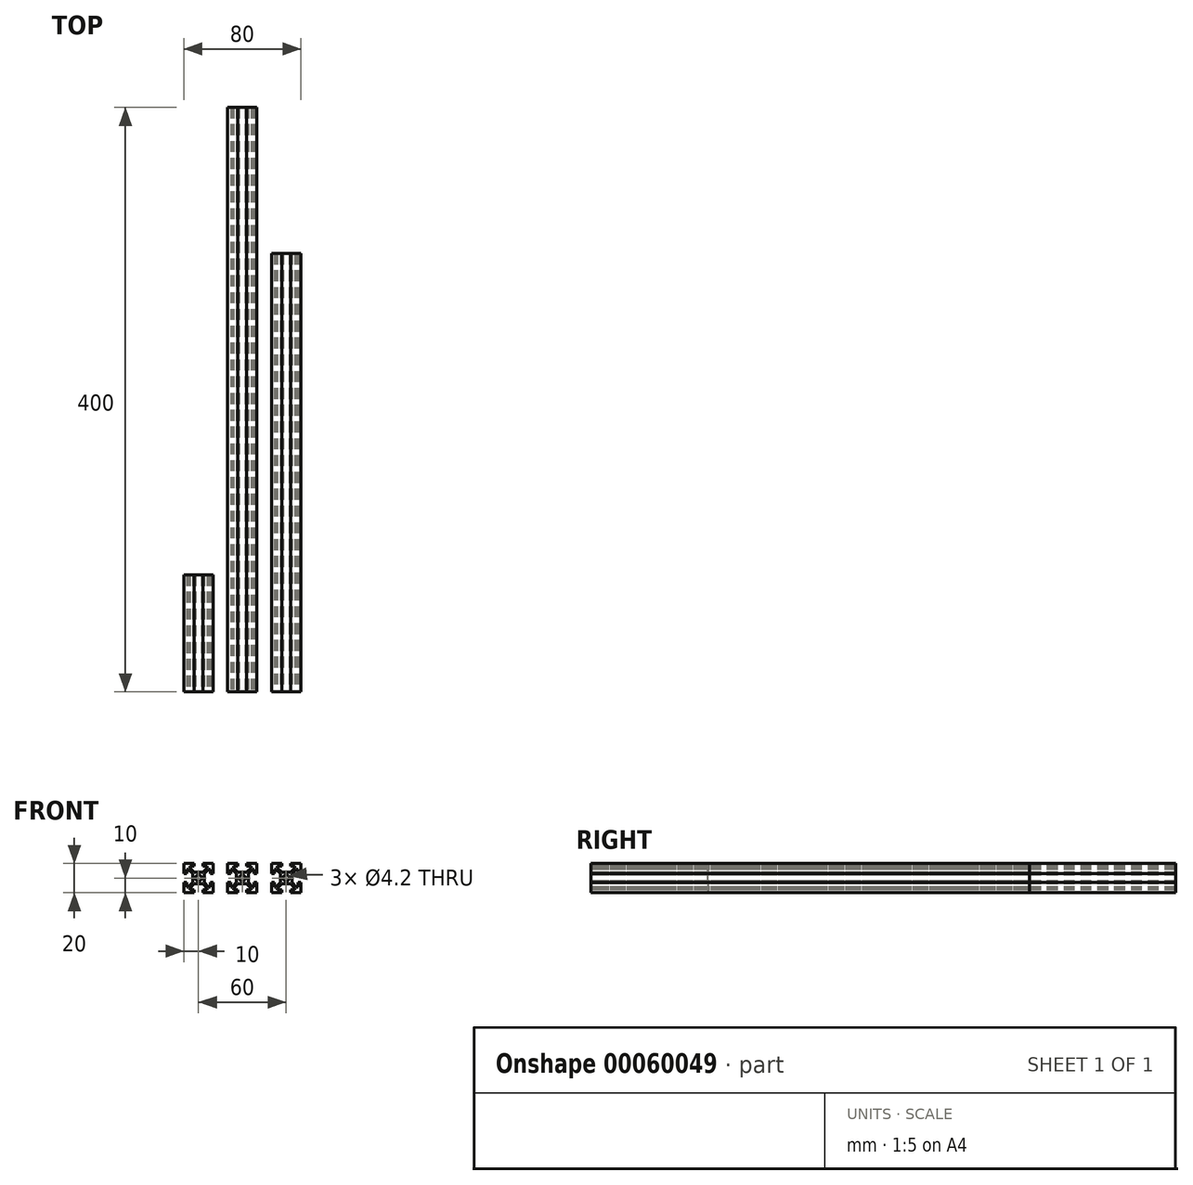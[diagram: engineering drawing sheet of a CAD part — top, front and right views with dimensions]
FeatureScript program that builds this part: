
annotation { "Feature Type Name" : "Feature", "Feature Type Description" : "" }
export const myFeature = defineFeature(function(context is Context, id is Id, definition is map)
    precondition{}
    {
        {
            var Q0;
            Q0=qCreatedBy(makeId("Front.planeOp"),FACE);
            var sketch = newSketch(context, id + "F0", { "sketchPlane" : qUnion([Q0])});
            skLineSegment(sketch, "E0", {"start": v(0, 4) * mm, "end": v(3, 4) * mm});
            skLineSegment(sketch, "E1", {"start": v(3, 4) * mm, "end": v(6, 7) * mm});
            skLineSegment(sketch, "E2", {"start": v(6, 7) * mm, "end": v(6, 8) * mm});
            skLineSegment(sketch, "E3", {"start": v(6, 8) * mm, "end": v(3, 8) * mm});
            skLineSegment(sketch, "E4", {"start": v(3, 8) * mm, "end": v(3, 10) * mm});
            skLineSegment(sketch, "E5", {"start": v(3, 10) * mm, "end": v(10, 10) * mm});
            skLineSegment(sketch, "E6", {"start": v(0, 0) * mm, "end": v(23.75, 23.75) * mm, "construction": true});
            skLineSegment(sketch, "E7.MirrorCS", {"start": v(8, 6) * mm, "end": v(8, 3) * mm});
            skLineSegment(sketch, "E8.MirrorCS", {"start": v(7, 6) * mm, "end": v(8, 6) * mm});
            skLineSegment(sketch, "E9.MirrorCS", {"start": v(8, 3) * mm, "end": v(10, 3) * mm});
            skLineSegment(sketch, "E10.MirrorCS", {"start": v(4, 0) * mm, "end": v(4, 3) * mm});
            skLineSegment(sketch, "E11.MirrorCS", {"start": v(10, 3) * mm, "end": v(10, 10) * mm});
            skLineSegment(sketch, "E12.MirrorCS", {"start": v(4, 3) * mm, "end": v(7, 6) * mm});
            skLineSegment(sketch, "E13.MirrorCS", {"start": v(-4, 3) * mm, "end": v(-7, 6) * mm});
            skLineSegment(sketch, "E14.MirrorCS", {"start": v(-10, 3) * mm, "end": v(-10, 10) * mm});
            skLineSegment(sketch, "E15.MirrorCS", {"start": v(-4, 0) * mm, "end": v(-4, 3) * mm});
            skLineSegment(sketch, "E16.MirrorCS", {"start": v(-8, 3) * mm, "end": v(-10, 3) * mm});
            skLineSegment(sketch, "E17.MirrorCS", {"start": v(-7, 6) * mm, "end": v(-8, 6) * mm});
            skLineSegment(sketch, "E18.MirrorCS", {"start": v(-8, 6) * mm, "end": v(-8, 3) * mm});
            skLineSegment(sketch, "E19.MirrorCS", {"start": v(-3, 10) * mm, "end": v(-10, 10) * mm});
            skLineSegment(sketch, "E20.MirrorCS", {"start": v(0, 4) * mm, "end": v(-3, 4) * mm});
            skLineSegment(sketch, "E21.MirrorCS", {"start": v(-3, 4) * mm, "end": v(-6, 7) * mm});
            skLineSegment(sketch, "E22.MirrorCS", {"start": v(-3, 8) * mm, "end": v(-3, 10) * mm});
            skLineSegment(sketch, "E23.MirrorCS", {"start": v(-6, 8) * mm, "end": v(-3, 8) * mm});
            skLineSegment(sketch, "E24.MirrorCS", {"start": v(-6, 7) * mm, "end": v(-6, 8) * mm});
            skLineSegment(sketch, "E25.MirrorCS", {"start": v(-6, -7) * mm, "end": v(-6, -8) * mm});
            skLineSegment(sketch, "E26.MirrorCS", {"start": v(-7, -6) * mm, "end": v(-8, -6) * mm});
            skLineSegment(sketch, "E27.MirrorCS", {"start": v(6, -7) * mm, "end": v(6, -8) * mm});
            skLineSegment(sketch, "E28.MirrorCS", {"start": v(7, -6) * mm, "end": v(8, -6) * mm});
            skLineSegment(sketch, "E29.MirrorCS", {"start": v(-3, -4) * mm, "end": v(-6, -7) * mm});
            skLineSegment(sketch, "E30.MirrorCS", {"start": v(-3, -10) * mm, "end": v(-10, -10) * mm});
            skLineSegment(sketch, "E31.MirrorCS", {"start": v(-4, -3) * mm, "end": v(-7, -6) * mm});
            skLineSegment(sketch, "E32.MirrorCS", {"start": v(-10, -3) * mm, "end": v(-10, -10) * mm});
            skLineSegment(sketch, "E33.MirrorCS", {"start": v(-4, 0) * mm, "end": v(-4, -3) * mm});
            skLineSegment(sketch, "E34.MirrorCS", {"start": v(0, -4) * mm, "end": v(3, -4) * mm});
            skLineSegment(sketch, "E35.MirrorCS", {"start": v(3, -4) * mm, "end": v(6, -7) * mm});
            skLineSegment(sketch, "E36.MirrorCS", {"start": v(3, -10) * mm, "end": v(10, -10) * mm});
            skLineSegment(sketch, "E37.MirrorCS", {"start": v(-8, -3) * mm, "end": v(-10, -3) * mm});
            skLineSegment(sketch, "E38.MirrorCS", {"start": v(-8, -6) * mm, "end": v(-8, -3) * mm});
            skLineSegment(sketch, "E39.MirrorCS", {"start": v(0, -4) * mm, "end": v(-3, -4) * mm});
            skLineSegment(sketch, "E40.MirrorCS", {"start": v(-3, -8) * mm, "end": v(-3, -10) * mm});
            skLineSegment(sketch, "E41.MirrorCS", {"start": v(4, 0) * mm, "end": v(4, -3) * mm});
            skLineSegment(sketch, "E42.MirrorCS", {"start": v(10, -3) * mm, "end": v(10, -10) * mm});
            skLineSegment(sketch, "E43.MirrorCS", {"start": v(8, -3) * mm, "end": v(10, -3) * mm});
            skLineSegment(sketch, "E44.MirrorCS", {"start": v(8, -6) * mm, "end": v(8, -3) * mm});
            skLineSegment(sketch, "E45.MirrorCS", {"start": v(4, -3) * mm, "end": v(7, -6) * mm});
            skLineSegment(sketch, "E46.MirrorCS", {"start": v(3, -8) * mm, "end": v(3, -10) * mm});
            skLineSegment(sketch, "E47.MirrorCS", {"start": v(-6, -8) * mm, "end": v(-3, -8) * mm});
            skLineSegment(sketch, "E48.MirrorCS", {"start": v(6, -8) * mm, "end": v(3, -8) * mm});
            skCircle(sketch, "E49", {"center": v(0, 0) * mm, "radius": 2.1 * mm});
            skSolve(sketch);
        }
        {
            var Q0;
            Q0=makeQuery(id+"F0.imprint","IMPRINT",FACE,{"disambiguationData":[TD([[makeQuery(id+"F0.imprint","IMPRINT",EDGE,{"derivedFrom":sQuery(id+"F0.wireOp",EDGE,"E0")}),-1.0]])]});
            extrude(context, id + "F1", {"entities" : qUnion([Q0]), "oppositeDirection" : true, "depth" : 80 * mm});
        }
        {
            var Q0;
            Q0=makeQuery(id+"F1.opExtrude","SWEPT_BODY",BODY,{"disambiguationData":[OSD([sQuery(id+"F0.wireOp",EDGE,"E0"),sQuery(id+"F0.wireOp",EDGE,"E1"),sQuery(id+"F0.wireOp",EDGE,"E2"),sQuery(id+"F0.wireOp",EDGE,"E3"),sQuery(id+"F0.wireOp",EDGE,"E4"),sQuery(id+"F0.wireOp",EDGE,"E5"),sQuery(id+"F0.wireOp",EDGE,"E7.MirrorCS"),sQuery(id+"F0.wireOp",EDGE,"E8.MirrorCS"),sQuery(id+"F0.wireOp",EDGE,"E9.MirrorCS"),sQuery(id+"F0.wireOp",EDGE,"E10.MirrorCS"),sQuery(id+"F0.wireOp",EDGE,"E11.MirrorCS"),sQuery(id+"F0.wireOp",EDGE,"E12.MirrorCS"),sQuery(id+"F0.wireOp",EDGE,"E13.MirrorCS"),sQuery(id+"F0.wireOp",EDGE,"E14.MirrorCS"),sQuery(id+"F0.wireOp",EDGE,"E15.MirrorCS"),sQuery(id+"F0.wireOp",EDGE,"E16.MirrorCS"),sQuery(id+"F0.wireOp",EDGE,"E17.MirrorCS"),sQuery(id+"F0.wireOp",EDGE,"E18.MirrorCS"),sQuery(id+"F0.wireOp",EDGE,"E19.MirrorCS"),sQuery(id+"F0.wireOp",EDGE,"E20.MirrorCS"),sQuery(id+"F0.wireOp",EDGE,"E21.MirrorCS"),sQuery(id+"F0.wireOp",EDGE,"E22.MirrorCS"),sQuery(id+"F0.wireOp",EDGE,"E23.MirrorCS"),sQuery(id+"F0.wireOp",EDGE,"E24.MirrorCS"),sQuery(id+"F0.wireOp",EDGE,"E25.MirrorCS"),sQuery(id+"F0.wireOp",EDGE,"E26.MirrorCS"),sQuery(id+"F0.wireOp",EDGE,"E27.MirrorCS"),sQuery(id+"F0.wireOp",EDGE,"E28.MirrorCS"),sQuery(id+"F0.wireOp",EDGE,"E29.MirrorCS"),sQuery(id+"F0.wireOp",EDGE,"E30.MirrorCS"),sQuery(id+"F0.wireOp",EDGE,"E31.MirrorCS"),sQuery(id+"F0.wireOp",EDGE,"E32.MirrorCS"),sQuery(id+"F0.wireOp",EDGE,"E33.MirrorCS"),sQuery(id+"F0.wireOp",EDGE,"E34.MirrorCS"),sQuery(id+"F0.wireOp",EDGE,"E35.MirrorCS"),sQuery(id+"F0.wireOp",EDGE,"E36.MirrorCS"),sQuery(id+"F0.wireOp",EDGE,"E37.MirrorCS"),sQuery(id+"F0.wireOp",EDGE,"E38.MirrorCS"),sQuery(id+"F0.wireOp",EDGE,"E39.MirrorCS"),sQuery(id+"F0.wireOp",EDGE,"E40.MirrorCS"),sQuery(id+"F0.wireOp",EDGE,"E41.MirrorCS"),sQuery(id+"F0.wireOp",EDGE,"E42.MirrorCS"),sQuery(id+"F0.wireOp",EDGE,"E43.MirrorCS"),sQuery(id+"F0.wireOp",EDGE,"E44.MirrorCS"),sQuery(id+"F0.wireOp",EDGE,"E45.MirrorCS"),sQuery(id+"F0.wireOp",EDGE,"E46.MirrorCS"),sQuery(id+"F0.wireOp",EDGE,"E47.MirrorCS"),sQuery(id+"F0.wireOp",EDGE,"E48.MirrorCS"),sQuery(id+"F0.wireOp",EDGE,"E49")])]});
            transform(context, id + "F2", {"entities" : qUnion([Q0]), "transformType" : TransformType.TRANSLATION_3D, "dx" : -30 * mm, "dy" : 0 * mm, "dz" : 0 * mm, "makeCopy" : false});
        }
        {
            var Q0;
            Q0 = qSketchRegion(id + "F0", true);
            extrude(context, id + "F3", {"entities" : qUnion([Q0]), "oppositeDirection" : true, "depth" : 300 * mm});
        }
        {
            var Q0;
            Q0=makeQuery(id+"F3.opExtrude","SWEPT_BODY",BODY,{"disambiguationData":[OSD([sQuery(id+"F0.wireOp",EDGE,"E0"),sQuery(id+"F0.wireOp",EDGE,"E1"),sQuery(id+"F0.wireOp",EDGE,"E2"),sQuery(id+"F0.wireOp",EDGE,"E3"),sQuery(id+"F0.wireOp",EDGE,"E4"),sQuery(id+"F0.wireOp",EDGE,"E5"),sQuery(id+"F0.wireOp",EDGE,"E7.MirrorCS"),sQuery(id+"F0.wireOp",EDGE,"E8.MirrorCS"),sQuery(id+"F0.wireOp",EDGE,"E9.MirrorCS"),sQuery(id+"F0.wireOp",EDGE,"E10.MirrorCS"),sQuery(id+"F0.wireOp",EDGE,"E11.MirrorCS"),sQuery(id+"F0.wireOp",EDGE,"E12.MirrorCS"),sQuery(id+"F0.wireOp",EDGE,"E13.MirrorCS"),sQuery(id+"F0.wireOp",EDGE,"E14.MirrorCS"),sQuery(id+"F0.wireOp",EDGE,"E15.MirrorCS"),sQuery(id+"F0.wireOp",EDGE,"E16.MirrorCS"),sQuery(id+"F0.wireOp",EDGE,"E17.MirrorCS"),sQuery(id+"F0.wireOp",EDGE,"E18.MirrorCS"),sQuery(id+"F0.wireOp",EDGE,"E19.MirrorCS"),sQuery(id+"F0.wireOp",EDGE,"E20.MirrorCS"),sQuery(id+"F0.wireOp",EDGE,"E21.MirrorCS"),sQuery(id+"F0.wireOp",EDGE,"E22.MirrorCS"),sQuery(id+"F0.wireOp",EDGE,"E23.MirrorCS"),sQuery(id+"F0.wireOp",EDGE,"E24.MirrorCS"),sQuery(id+"F0.wireOp",EDGE,"E25.MirrorCS"),sQuery(id+"F0.wireOp",EDGE,"E26.MirrorCS"),sQuery(id+"F0.wireOp",EDGE,"E27.MirrorCS"),sQuery(id+"F0.wireOp",EDGE,"E28.MirrorCS"),sQuery(id+"F0.wireOp",EDGE,"E29.MirrorCS"),sQuery(id+"F0.wireOp",EDGE,"E30.MirrorCS"),sQuery(id+"F0.wireOp",EDGE,"E31.MirrorCS"),sQuery(id+"F0.wireOp",EDGE,"E32.MirrorCS"),sQuery(id+"F0.wireOp",EDGE,"E33.MirrorCS"),sQuery(id+"F0.wireOp",EDGE,"E34.MirrorCS"),sQuery(id+"F0.wireOp",EDGE,"E35.MirrorCS"),sQuery(id+"F0.wireOp",EDGE,"E36.MirrorCS"),sQuery(id+"F0.wireOp",EDGE,"E37.MirrorCS"),sQuery(id+"F0.wireOp",EDGE,"E38.MirrorCS"),sQuery(id+"F0.wireOp",EDGE,"E39.MirrorCS"),sQuery(id+"F0.wireOp",EDGE,"E40.MirrorCS"),sQuery(id+"F0.wireOp",EDGE,"E41.MirrorCS"),sQuery(id+"F0.wireOp",EDGE,"E42.MirrorCS"),sQuery(id+"F0.wireOp",EDGE,"E43.MirrorCS"),sQuery(id+"F0.wireOp",EDGE,"E44.MirrorCS"),sQuery(id+"F0.wireOp",EDGE,"E45.MirrorCS"),sQuery(id+"F0.wireOp",EDGE,"E46.MirrorCS"),sQuery(id+"F0.wireOp",EDGE,"E47.MirrorCS"),sQuery(id+"F0.wireOp",EDGE,"E48.MirrorCS"),sQuery(id+"F0.wireOp",EDGE,"E49")])]});
            transform(context, id + "F4", {"entities" : qUnion([Q0]), "transformType" : TransformType.TRANSLATION_3D, "dx" : 30 * mm, "dy" : 0 * mm, "dz" : 0 * mm, "makeCopy" : false});
        }
        {
            var Q0;
            Q0 = qSketchRegion(id + "F0", true);
            extrude(context, id + "F5", {"entities" : qUnion([Q0]), "oppositeDirection" : true, "depth" : 400 * mm});
        }
        {
            var Q0;
            Q0=makeQuery(id+"F3.opExtrude","SWEPT_FACE",FACE,{"disambiguationData":[OSD([sQuery(id+"F0.wireOp",EDGE,"E5")])]});
            var sketch = newSketch(context, id + "F6", { "sketchPlane" : qUnion([Q0])});
            skLineSegment(sketch, "E50.0", {"start": v(40, 300) * mm, "end": v(40, 0) * mm, "construction": true});
            skPoint(sketch, "E51", {"position": v(40, 200) * mm});
            skPoint(sketch, "E52", {"position": v(40, 100) * mm});
            skSolve(sketch);
        }
        {
            var Q0;
            Q0=makeQuery(id+"F5.opExtrude","SWEPT_FACE",FACE,{"disambiguationData":[OSD([sQuery(id+"F0.wireOp",EDGE,"E19.MirrorCS")])]});
            var sketch = newSketch(context, id + "F7", { "sketchPlane" : qUnion([Q0])});
            skLineSegment(sketch, "E53", {"start": v(-10, 200) * mm, "end": v(10, 200) * mm, "construction": true});
            skPoint(sketch, "E54", {"position": v(0, 200) * mm});
            skSolve(sketch);
        }
    });
